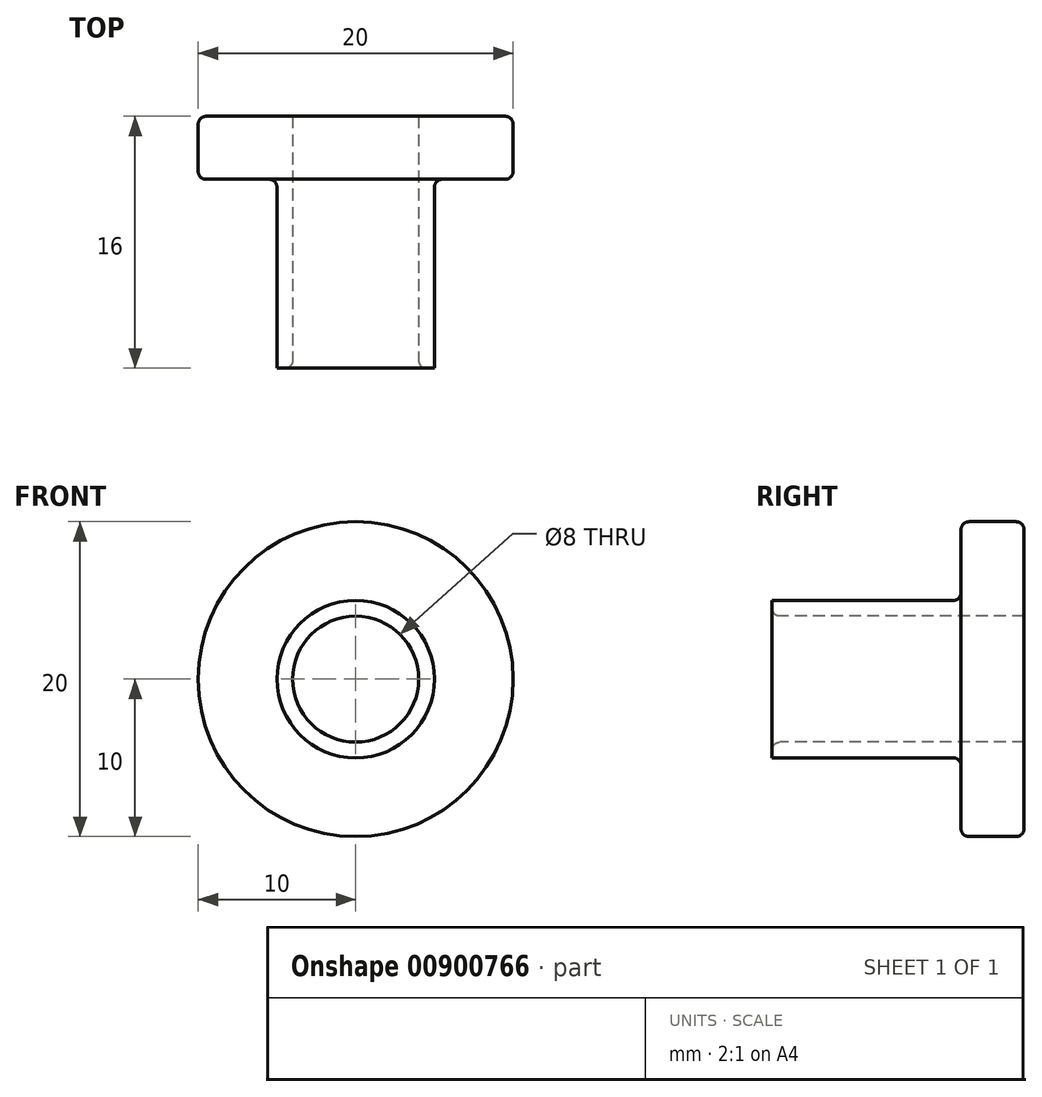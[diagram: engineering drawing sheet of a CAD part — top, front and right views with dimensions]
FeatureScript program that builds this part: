
annotation { "Feature Type Name" : "Feature", "Feature Type Description" : "" }
export const myFeature = defineFeature(function(context is Context, id is Id, definition is map)
    precondition{}
    {
        {
            var Q0;
            Q0=qCreatedBy(makeId("Right.planeOp"),FACE);
            var sketch = newSketch(context, id + "F0", { "sketchPlane" : qUnion([Q0])});
            skLineSegment(sketch, "E0", {"start": v(0, 4) * mm, "end": v(-16, 4) * mm});
            skLineSegment(sketch, "E1", {"start": v(-16, 4) * mm, "end": v(-16, 5) * mm});
            skLineSegment(sketch, "E2", {"start": v(-16, 5) * mm, "end": v(-4, 5) * mm});
            skLineSegment(sketch, "E3", {"start": v(-4, 5) * mm, "end": v(-4, 10) * mm});
            skLineSegment(sketch, "E4", {"start": v(0, 4) * mm, "end": v(0, 10) * mm});
            skLineSegment(sketch, "E5", {"start": v(0, 10) * mm, "end": v(-4, 10) * mm});
            skLineSegment(sketch, "E6", {"start": v(-23.38, 0) * mm, "end": v(23.38, 0) * mm, "construction": true});
            skSolve(sketch);
        }
        {
            var Q0;
            Q0 = qSketchRegion(id + "F0", true);
            var Q1;
            Q1=sQuery(id+"F0.wireOp",EDGE,"E6");
            revolve(context, id + "F1", {"surfaceOperationType" : NewSurfaceOperationType.NEW, "entities" : qUnion([Q0]), "axis" : qUnion([Q1]), "revolveType" : RevolveType.FULL});
        }
        {
            var Q0;
            Q0=makeQuery(id+"F1.opRevolve","SWEPT_EDGE",EDGE,{"disambiguationData":[OSD([sQuery(id+"F0.wireOp",EDGE,"E0"),sQuery(id+"F0.wireOp",EDGE,"E1")])]});
            var Q1;
            Q1=makeQuery(id+"F1.opRevolve","SWEPT_EDGE",EDGE,{"disambiguationData":[OSD([sQuery(id+"F0.wireOp",EDGE,"E2"),sQuery(id+"F0.wireOp",EDGE,"E3")])]});
            var Q2;
            Q2=makeQuery(id+"F1.opRevolve","SWEPT_EDGE",EDGE,{"disambiguationData":[OSD([sQuery(id+"F0.wireOp",EDGE,"E3"),sQuery(id+"F0.wireOp",EDGE,"E5")])]});
            var Q3;
            Q3=makeQuery(id+"F1.opRevolve","SWEPT_EDGE",EDGE,{"disambiguationData":[OSD([sQuery(id+"F0.wireOp",EDGE,"E4"),sQuery(id+"F0.wireOp",EDGE,"E5")])]});
            fillet(context, id + "F2", {"entities" : qUnion([Q0, Q1, Q2, Q3]), "radius" : 0.5 * mm, "tangentPropagation" : true, "allowEdgeOverflow" : false});
        }
    });
